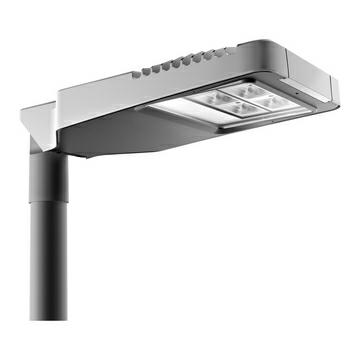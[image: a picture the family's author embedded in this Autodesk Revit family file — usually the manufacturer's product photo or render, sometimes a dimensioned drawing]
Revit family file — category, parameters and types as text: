
# Revit family: Lighting-Stradale-GEWISS-ROAD[5]MINI-LED_OTTICA_WIDE-W_NEMA-ZAGA
name_source: partatom
category: Apparecchi per illuminazione
units: mm (PartAtom-declared; Revit-internal decimal feet)

## family parameters
Basato su piano di lavoro = No
Condiviso = No
Punto di calcolo locali = No
Quota connettore circolare = Usa diametro
Sempre verticale = Sì
Sorgente d'illuminazione = No
Taglio con vuoti quando caricato = No
Tipo di parte = Normale

## types (1)
- Lighting-Stradale-GEWISS-ROAD[5]MINI-LED_OTTICA_WIDE-W_NEMA-ZAGA
    Alimentatore = Incluso
    Apparecchio a ridotta temperatura superficiale = -
    Applicazione = Esterno
    Cablaggio = Sezionatore
    Caratteristiche elettriche e gestione della luce = -
    Caratteristiche ottiche e illuminotecniche = -
    Carico apparente = 28 VA
    Catalogo = LIGHTING
    Catalogo Serie = ROAD [5]
    Certificazione DIN 18032-3 = -
    Certificazioni e classificazioni = -
    Classe fotobiologica = RG0
    Classe isolamento = II
    Classificazione: = -
    Codice Electrocod = 244C
    Codice digitale univoco (Datamatrix) = Attualmente non presente
    Colore = Grigio grafite
    Commenti sul wattaggio = 28W
    Contesto = Illuminazione stradale e parcheggi
    Controllo abbagliamento e luminanza = G*4 - ULOR = 0
    Corpo = Alluminio pressofuso
    Corrente di pilotaggio. = 0,5A
    Descrizione = GWR5252ZW - ROAD5 MINI WIDE 2M 4000K 0,50A CL2 W ZHA
    Dispositivo di protezione = DM 10KV / CM 10KV
    Distanza minima dall'oggetto illuminato = 1M
    Durata di vita = L90B10 (Tq+25°C) = 100.000 h
    Efficienza luminosa (lm/W) = 111
    Finitura colore = Verniciato a polveri
    Fissaggio = Testa palo - Sbraccio
    Frequenza nominale (Hz) = 50 / 60
    Gancio di chiusura = Maniglia frontale integrata
    Garanzia = 5 anni
    Grado di protezione = IP66
    Gruppo ottico = Riflettore in PC metallizzato
    Guarnizioni = silicone antinvecchiamento
    IDF = abbb80bf-f95b-43c6-b7d8-d8e1b7f34275
    IDT = 6ace804b625941958a80978d94961bce
    IPEA = STRADALE = A3+ // GRANDI AREE = A4+ // CICLOPEDONALI = A++ // AREE VERDI = A++ // CENTRO STORICO = A6+
    Immagine tipo = GWR5276M.jpg
    Inclinazione = -20° ÷ +10° sbraccio - -10° ÷ +20° testa palo
    Indice di resa cromatica = CRI-70
    Informazioni generali = -
    Installazione e manutenzione = -
    LED Life time (L80B10) = 100000H
    Lampada: = LED
    Lumen output (lm) = 8100
    Materiali = -
    Modello = GWR5252ZW
    Norma di riferimento = EN 60598-2-3, EN 60598-1 IEC/TR 62778
    Numero moduli = 2 (2x3 LED)
    Ottica = WIDE
    Peso (kg): = 6,59999999999999
    Potenza assorbita : = 73 W @ 0.5A
    Potenza di sistema = 73W
    Produttore = GEWISS S.p.A.
    Regolazione inclinazione = -20° ÷ +10° sbraccio - -10° ÷ +20° testa palo
    Resistenza agli urti = IK08
    Resistenza al filo incandescente = -
    Resistenza alle sovratensioni = 10 KV in modalità comune
    SEO = Stradale
    Scheda Tecnica = https://www.gewiss.com
    Schermo = Vetro piano temperato spessore 4mm
    Sistema di controllo = Telegestione con modulo Zhaga
    Sostituibilità gruppo ottico = Non disponibile
    Sostituibilità piastra di cablaggio = Non disponibile
    Superficie massima esposta al vento = 0,149999999999999M2
    Superficie massima esposta al vento : = 0,15 m²
    Temperatura di colore = 4000K
    Temperatura di colore: = 4000 K (CRI>70)
    Temperatura di esercizio = -25 +30 °C
    Temperatura di stoccaggio = -
    Temperatura di utilizzo = -25 +30 °C
    Tensione = 220 / 240 V - 50 / 60 Hz
    Tensione di alimentazione = 220 - 240 V
    Tipo alimentatore = Driver Led in corrente continua
    Tipo di apparecchio = Apparecchiatura stradale a LED
    Tipo di installazione e montaggio = Testa palo - Sbraccio
    Tipologia = Biregime
    Tipologia sorgente luminosa = LED - Non sostituibile
    Tolleranza cromatica = SDCM = 5
    URL = https://www.gewiss.com
    Vano di alimentazione = Integrato
    Versione file RFA = 20.11
    Viti esterne = Acciaio inox

## geometry (parser evidence)
native form markers: Blend x2
no freeform markers — native parametric forms only
